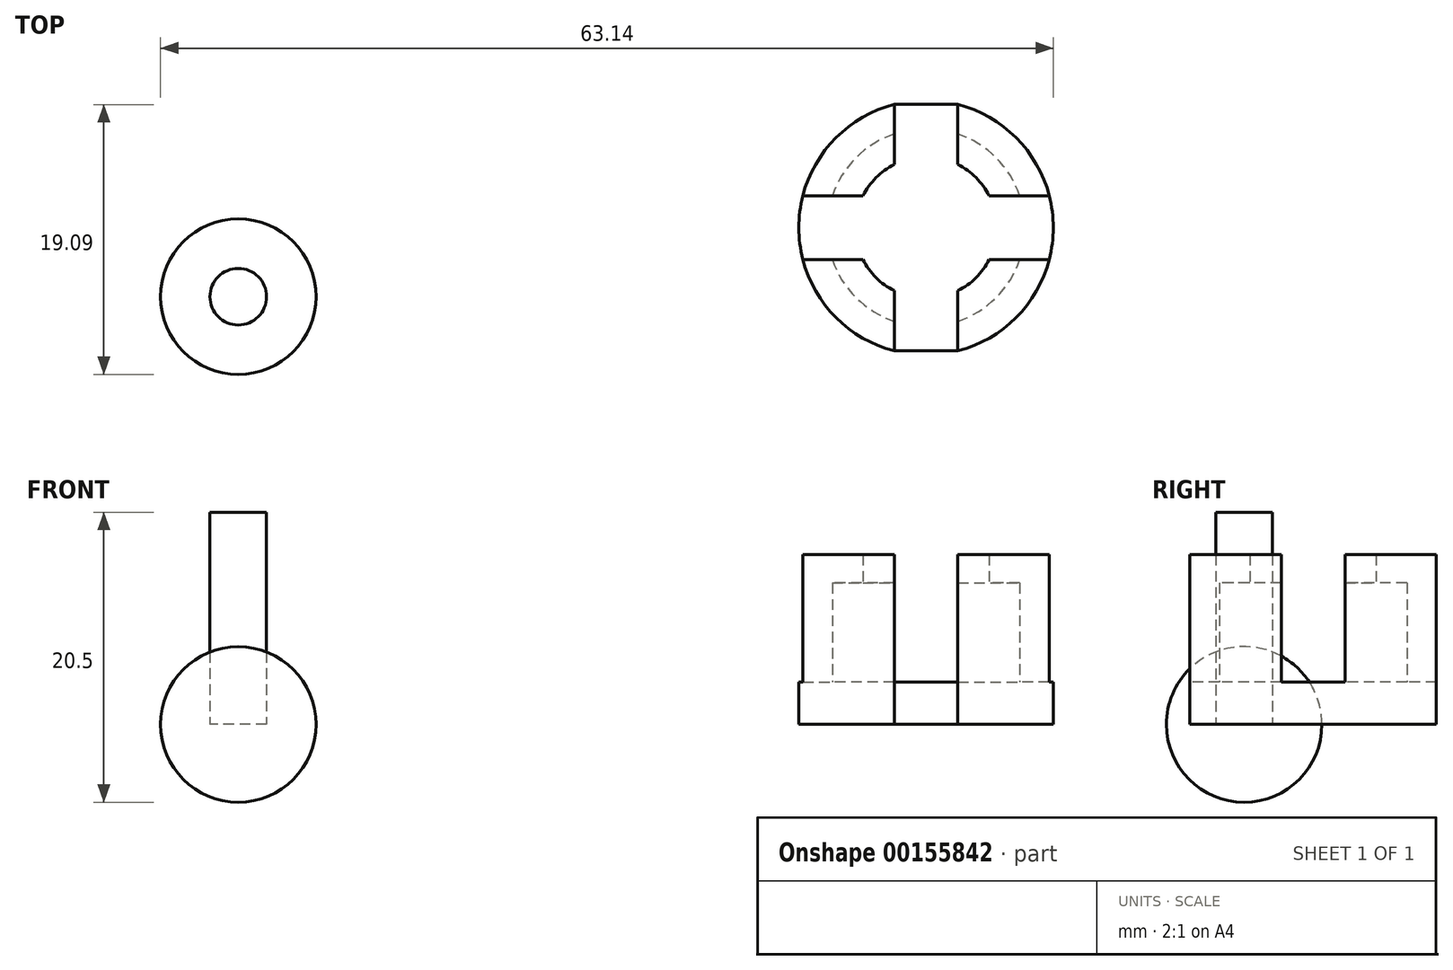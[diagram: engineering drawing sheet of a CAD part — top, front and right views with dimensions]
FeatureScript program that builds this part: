
annotation { "Feature Type Name" : "Feature", "Feature Type Description" : "" }
export const myFeature = defineFeature(function(context is Context, id is Id, definition is map)
    precondition{}
    {
        {
            var Q0;
            Q0=qCreatedBy(makeId("Top.planeOp"),FACE);
            var sketch = newSketch(context, id + "F0", { "sketchPlane" : qUnion([Q0])});
            skArc(sketch, "E0", {"start": v(-2.25, 4.47) * mm, "mid": v(-5, 0) * mm, "end": v(-2.25, -4.47) * mm});
            skArc(sketch, "E1.0", {"start": v(-2.25, 8.71) * mm, "mid": v(-9, 0) * mm, "end": v(-2.25, -8.71) * mm});
            skLineSegment(sketch, "E2", {"start": v(-2.25, 8.71) * mm, "end": v(-2.25, 4.47) * mm});
            skLineSegment(sketch, "E3", {"start": v(-2.25, -4.47) * mm, "end": v(-2.25, -8.71) * mm});
            skLineSegment(sketch, "E4.MirrorCS", {"start": v(2.25, 8.71) * mm, "end": v(2.25, 4.47) * mm});
            skArc(sketch, "E5.MirrorCS", {"start": v(2.25, 8.71) * mm, "mid": v(9, 0) * mm, "end": v(2.25, -8.71) * mm});
            skArc(sketch, "E6.MirrorCS", {"start": v(2.25, 4.47) * mm, "mid": v(5, 0) * mm, "end": v(2.25, -4.47) * mm});
            skLineSegment(sketch, "E7.MirrorCS", {"start": v(2.25, -4.47) * mm, "end": v(2.25, -8.71) * mm});
            skLineSegment(sketch, "E8", {"start": v(-8.71, -2.25) * mm, "end": v(-4.47, -2.25) * mm});
            skLineSegment(sketch, "E9", {"start": v(-8.71, 2.25) * mm, "end": v(-4.47, 2.25) * mm});
            skLineSegment(sketch, "E10.MirrorCS", {"start": v(8.71, -2.25) * mm, "end": v(4.47, -2.25) * mm});
            skLineSegment(sketch, "E11.MirrorCS", {"start": v(8.71, 2.25) * mm, "end": v(4.47, 2.25) * mm});
            skSolve(sketch);
        }
        {
            var Q0;
            Q0=qCreatedBy(makeId("Top.planeOp"),FACE);
            var sketch = newSketch(context, id + "F1", { "sketchPlane" : qUnion([Q0])});
            skArc(sketch, "E12", {"start": v(-48.64, 0.62) * mm, "mid": v(-54.14, -4.88) * mm, "end": v(-48.64, -10.38) * mm});
            skLineSegment(sketch, "E13", {"start": v(-48.64, 0.62) * mm, "end": v(-48.64, -10.38) * mm});
            skSolve(sketch);
        }
        {
            var Q0;
            Q0=makeQuery(id+"F1.imprint","IMPRINT",FACE,{"disambiguationData":[TD([[makeQuery(id+"F1.imprint","IMPRINT",EDGE,{"derivedFrom":sQuery(id+"F1.wireOp",EDGE,"E12")}),1.0]])]});
            var Q1;
            Q1=sQuery(id+"F1.wireOp",EDGE,"E13");
            revolve(context, id + "F2", {"entities" : qUnion([Q0]), "axis" : qUnion([Q1]), "revolveType" : RevolveType.FULL});
        }
        {
            var Q0;
            Q0=qCreatedBy(makeId("Top.planeOp"),FACE);
            var sketch = newSketch(context, id + "F3", { "sketchPlane" : qUnion([Q0])});
            skPoint(sketch, "E14.0", {"position": v(-48.64, -4.88) * mm});
            skCircle(sketch, "E15", {"center": v(-48.64, -4.88) * mm, "radius": 2 * mm});
            skSolve(sketch);
        }
        {
            var Q0;
            Q0=makeQuery(id+"F3.imprint","IMPRINT",FACE,{"disambiguationData":[TD([[makeQuery(id+"F3.imprint","IMPRINT",EDGE,{"derivedFrom":sQuery(id+"F3.wireOp",EDGE,"E15")}),1.0]])]});
            extrude(context, id + "F4", {"entities" : qUnion([Q0]), "depth" : 15 * mm});
        }
        {
            var Q0;
            Q0=qCreatedBy(makeId("Top.planeOp"),FACE);
            var sketch = newSketch(context, id + "F5", { "sketchPlane" : qUnion([Q0])});
            skArc(sketch, "E16.0", {"start": v(-2.25, 4.47) * mm, "mid": v(-5, 0) * mm, "end": v(-2.25, -4.47) * mm});
            skArc(sketch, "E17.0", {"start": v(-2.25, 8.71) * mm, "mid": v(-9, 0) * mm, "end": v(-2.25, -8.71) * mm});
            skLineSegment(sketch, "E18.0", {"start": v(-8.71, 2.25) * mm, "end": v(-4.47, 2.25) * mm});
            skLineSegment(sketch, "E19.0", {"start": v(-8.71, -2.25) * mm, "end": v(-4.47, -2.25) * mm});
            skLineSegment(sketch, "E20.0", {"start": v(-2.25, -4.47) * mm, "end": v(-2.25, -8.71) * mm});
            skLineSegment(sketch, "E21.0", {"start": v(2.25, -4.47) * mm, "end": v(2.25, -8.71) * mm});
            skArc(sketch, "E22.0", {"start": v(2.25, 4.47) * mm, "mid": v(5, 0) * mm, "end": v(2.25, -4.47) * mm});
            skArc(sketch, "E23.0", {"start": v(2.25, 8.71) * mm, "mid": v(9, 0) * mm, "end": v(2.25, -8.71) * mm});
            skLineSegment(sketch, "E24.0", {"start": v(8.71, -2.25) * mm, "end": v(4.47, -2.25) * mm});
            skLineSegment(sketch, "E25.0", {"start": v(8.71, 2.25) * mm, "end": v(4.47, 2.25) * mm});
            skLineSegment(sketch, "E26.0", {"start": v(2.25, 8.71) * mm, "end": v(2.25, 4.47) * mm});
            skLineSegment(sketch, "E27.0", {"start": v(-2.25, 8.71) * mm, "end": v(-2.25, 4.47) * mm});
            skLineSegment(sketch, "E28", {"start": v(-8.71, 2.25) * mm, "end": v(-8.71, -2.25) * mm});
            skLineSegment(sketch, "E29", {"start": v(8.71, 2.25) * mm, "end": v(8.71, -2.25) * mm});
            skLineSegment(sketch, "E30", {"start": v(-2.25, 8.71) * mm, "end": v(2.25, 8.71) * mm});
            skLineSegment(sketch, "E31", {"start": v(-2.25, -8.71) * mm, "end": v(2.25, -8.71) * mm});
            skSolve(sketch);
        }
        {
            var Q0;
            {var subQ2=sQuery(id+"F5.wireOp",EDGE,"E18.0");Q0=makeQuery(id+"F5.imprint","IMPRINT",FACE,{"disambiguationData":[TD([[makeQuery(id+"F5.imprint","IMPRINT",EDGE,{"derivedFrom":subQ2}),1.0]])]});}
            var Q1;
            {var subQ0=sQuery(id+"F0.wireOp",EDGE,"E8");Q1=makeQuery(id+"F0.imprint","IMPRINT",FACE,{"disambiguationData":[TD([[makeQuery(id+"F0.imprint","IMPRINT",EDGE,{"derivedFrom":subQ0}),1.0]])]});}
            var Q2;
            {var subQ2=sQuery(id+"F5.wireOp",EDGE,"E19.0");Q2=makeQuery(id+"F5.imprint","IMPRINT",FACE,{"disambiguationData":[TD([[makeQuery(id+"F5.imprint","IMPRINT",EDGE,{"derivedFrom":subQ2}),-1.0]])]});}
            var Q3;
            {var subQ0=sQuery(id+"F5.wireOp",EDGE,"E21.0");Q3=makeQuery(id+"F5.imprint","IMPRINT",FACE,{"disambiguationData":[TD([[makeQuery(id+"F5.imprint","IMPRINT",EDGE,{"derivedFrom":subQ0}),1.0]])]});}
            var Q4;
            {var subQ0=sQuery(id+"F0.wireOp",EDGE,"E10.MirrorCS");Q4=makeQuery(id+"F0.imprint","IMPRINT",FACE,{"disambiguationData":[TD([[makeQuery(id+"F0.imprint","IMPRINT",EDGE,{"derivedFrom":subQ0}),-1.0]])]});}
            var Q5;
            {var subQ0=sQuery(id+"F0.wireOp",EDGE,"E4.MirrorCS");Q5=makeQuery(id+"F0.imprint","IMPRINT",FACE,{"disambiguationData":[TD([[makeQuery(id+"F0.imprint","IMPRINT",EDGE,{"derivedFrom":subQ0}),1.0]])]});}
            var Q6;
            {var subQ8=sQuery(id+"F5.wireOp",EDGE,"E20.0");Q6=makeQuery(id+"F5.imprint","IMPRINT",FACE,{"disambiguationData":[TD([[makeQuery(id+"F5.imprint","IMPRINT",EDGE,{"derivedFrom":subQ8}),1.0]])]});}
            extrude(context, id + "F6", {"entities" : qUnion([Q0, Q1, Q2, Q3, Q4, Q5, Q6]), "operationType" : NewBodyOperationType.ADD, "depth" : 3 * mm});
        }
        {
            var Q0;
            Q0=makeQuery(id+"F6.boolean.opBoolean","MERGE",FACE,{"derivedFrom":[makeQuery(id+"F6.opExtrude","CAP_FACE",FACE,{"disambiguationData":[OSD([sQuery(id+"F0.wireOp",EDGE,"E0"),sQuery(id+"F0.wireOp",EDGE,"E1.0"),sQuery(id+"F0.wireOp",EDGE,"E8"),sQuery(id+"F0.wireOp",EDGE,"E9")])],"isStart":false}),makeQuery(id+"F6.opExtrude","CAP_FACE",FACE,{"disambiguationData":[OSD([sQuery(id+"F0.wireOp",EDGE,"E4.MirrorCS"),sQuery(id+"F0.wireOp",EDGE,"E5.MirrorCS"),sQuery(id+"F0.wireOp",EDGE,"E6.MirrorCS"),sQuery(id+"F0.wireOp",EDGE,"E10.MirrorCS")])],"isStart":false}),makeQuery(id+"F6.opExtrude","CAP_FACE",FACE,{"disambiguationData":[OSD([sQuery(id+"F5.wireOp",EDGE,"E16.0"),sQuery(id+"F5.wireOp",EDGE,"E17.0"),sQuery(id+"F5.wireOp",EDGE,"E18.0"),sQuery(id+"F5.wireOp",EDGE,"E19.0"),sQuery(id+"F5.wireOp",EDGE,"E22.0"),sQuery(id+"F5.wireOp",EDGE,"E23.0"),sQuery(id+"F5.wireOp",EDGE,"E24.0"),sQuery(id+"F5.wireOp",EDGE,"E26.0"),sQuery(id+"F5.wireOp",EDGE,"E30"),sQuery(id+"F5.wireOp",EDGE,"E31")])],"isStart":false})]});
            var sketch = newSketch(context, id + "F7", { "sketchPlane" : qUnion([Q0])});
            skArc(sketch, "E32.0", {"start": v(-2.25, 4.47) * mm, "mid": v(-5, 0) * mm, "end": v(-2.25, -4.47) * mm});
            skArc(sketch, "E33.0", {"start": v(-2.25, 8.71) * mm, "mid": v(-9, 0) * mm, "end": v(-2.25, -8.71) * mm});
            skLineSegment(sketch, "E34.0", {"start": v(-2.25, 8.71) * mm, "end": v(-2.25, 4.47) * mm});
            skLineSegment(sketch, "E35.0", {"start": v(-2.25, -4.47) * mm, "end": v(-2.25, -8.71) * mm});
            skLineSegment(sketch, "E36.0", {"start": v(2.25, -4.47) * mm, "end": v(2.25, -8.71) * mm});
            skLineSegment(sketch, "E37.0", {"start": v(2.25, 8.71) * mm, "end": v(2.25, 4.47) * mm});
            skArc(sketch, "E38.0", {"start": v(2.25, 8.71) * mm, "mid": v(9, 0) * mm, "end": v(2.25, -8.71) * mm});
            skArc(sketch, "E39.0", {"start": v(2.25, 4.47) * mm, "mid": v(5, 0) * mm, "end": v(2.25, -4.47) * mm});
            skLineSegment(sketch, "E40.0", {"start": v(-8.71, 2.25) * mm, "end": v(-4.47, 2.25) * mm});
            skLineSegment(sketch, "E41.0", {"start": v(-8.71, -2.25) * mm, "end": v(-4.47, -2.25) * mm});
            skLineSegment(sketch, "E42.0", {"start": v(8.71, -2.25) * mm, "end": v(4.47, -2.25) * mm});
            skLineSegment(sketch, "E43.0", {"start": v(8.71, 2.25) * mm, "end": v(4.47, 2.25) * mm});
            skArc(sketch, "E44.0", {"start": v(-2.25, 6.63) * mm, "mid": v(-7, 0) * mm, "end": v(-2.25, -6.63) * mm});
            skArc(sketch, "E45.MirrorCS", {"start": v(2.25, 6.63) * mm, "mid": v(7, 0) * mm, "end": v(2.25, -6.63) * mm});
            skSolve(sketch);
        }
        {
            var Q0;
            {var subQ1=sQuery(id+"F7.wireOp",EDGE,"E33.0");var subQ3=sQuery(id+"F7.wireOp",EDGE,"E40.0");var subQ4=makeQuery(id+"F7.imprint","INTERSECT",VERTEX,{"derivedFrom":[subQ1,subQ3]});Q0=makeQuery(id+"F7.imprint","IMPRINT",FACE,{"disambiguationData":[TD([[makeQuery(id+"F7.imprint","IMPRINT",EDGE,{"disambiguationData":[TD([[subQ4,-1.0]])],"derivedFrom":subQ3}),1.0]])]});}
            var Q1;
            {var subQ0=sQuery(id+"F7.wireOp",EDGE,"E38.0");var subQ5=sQuery(id+"F7.wireOp",EDGE,"E43.0");var subQ6=makeQuery(id+"F7.imprint","INTERSECT",VERTEX,{"derivedFrom":[subQ0,subQ5]});Q1=makeQuery(id+"F7.imprint","IMPRINT",FACE,{"disambiguationData":[TD([[makeQuery(id+"F7.imprint","IMPRINT",EDGE,{"disambiguationData":[TD([[subQ6,-1.0]])],"derivedFrom":subQ5}),-1.0]])]});}
            var Q2;
            {var subQ0=sQuery(id+"F7.wireOp",EDGE,"E38.0");var subQ5=sQuery(id+"F7.wireOp",EDGE,"E42.0");var subQ6=makeQuery(id+"F7.imprint","INTERSECT",VERTEX,{"derivedFrom":[subQ0,subQ5]});Q2=makeQuery(id+"F7.imprint","IMPRINT",FACE,{"disambiguationData":[TD([[makeQuery(id+"F7.imprint","IMPRINT",EDGE,{"disambiguationData":[TD([[subQ6,-1.0]])],"derivedFrom":subQ5}),1.0]])]});}
            var Q3;
            {var subQ1=sQuery(id+"F7.wireOp",EDGE,"E33.0");var subQ3=sQuery(id+"F7.wireOp",EDGE,"E41.0");var subQ4=makeQuery(id+"F7.imprint","INTERSECT",VERTEX,{"derivedFrom":[subQ1,subQ3]});Q3=makeQuery(id+"F7.imprint","IMPRINT",FACE,{"disambiguationData":[TD([[makeQuery(id+"F7.imprint","IMPRINT",EDGE,{"disambiguationData":[TD([[subQ4,-1.0]])],"derivedFrom":subQ3}),-1.0]])]});}
            extrude(context, id + "F8", {"entities" : qUnion([Q0, Q1, Q2, Q3]), "operationType" : NewBodyOperationType.ADD, "depth" : 7 * mm});
        }
        {
            var Q0;
            Q0=makeQuery(id+"F8.opExtrude","CAP_FACE",FACE,{"disambiguationData":[OSD([sQuery(id+"F7.wireOp",EDGE,"E33.0"),sQuery(id+"F7.wireOp",EDGE,"E34.0"),sQuery(id+"F7.wireOp",EDGE,"E40.0"),sQuery(id+"F7.wireOp",EDGE,"E44.0")])],"isStart":false});
            var sketch = newSketch(context, id + "F9", { "sketchPlane" : qUnion([Q0])});
            skArc(sketch, "E46.0", {"start": v(-2.25, 4.47) * mm, "mid": v(-5, 0) * mm, "end": v(-2.25, -4.47) * mm});
            skArc(sketch, "E47.0", {"start": v(2.25, 4.47) * mm, "mid": v(5, 0) * mm, "end": v(2.25, -4.47) * mm});
            skArc(sketch, "E48.0", {"start": v(2.25, 6.63) * mm, "mid": v(4.95, 4.95) * mm, "end": v(6.63, 2.25) * mm});
            skLineSegment(sketch, "E49.0", {"start": v(2.25, 8.71) * mm, "end": v(2.25, 4.47) * mm});
            skLineSegment(sketch, "E50.0", {"start": v(-8.71, 2.25) * mm, "end": v(-4.47, 2.25) * mm});
            skLineSegment(sketch, "E51.0", {"start": v(-2.25, 8.71) * mm, "end": v(-2.25, 4.47) * mm});
            skLineSegment(sketch, "E52.0", {"start": v(8.71, 2.25) * mm, "end": v(4.47, 2.25) * mm});
            skArc(sketch, "E53.0.0", {"start": v(8.71, -2.25) * mm, "mid": v(9, 0) * mm, "end": v(8.71, 2.25) * mm});
            skLineSegment(sketch, "E53.0.1", {"start": v(8.71, 2.25) * mm, "end": v(6.63, 2.25) * mm});
            skArc(sketch, "E53.0.2", {"start": v(6.63, 2.25) * mm, "mid": v(4.95, 4.95) * mm, "end": v(2.25, 6.63) * mm});
            skLineSegment(sketch, "E53.0.3", {"start": v(2.25, 6.63) * mm, "end": v(2.25, 8.71) * mm});
            skLineSegment(sketch, "E53.0.4", {"start": v(2.25, 8.71) * mm, "end": v(-2.25, 8.71) * mm});
            skLineSegment(sketch, "E53.0.5", {"start": v(-2.25, 8.71) * mm, "end": v(-2.25, 6.63) * mm});
            skArc(sketch, "E53.0.6", {"start": v(-2.25, 6.63) * mm, "mid": v(-4.95, 4.95) * mm, "end": v(-6.63, 2.25) * mm});
            skLineSegment(sketch, "E53.0.7", {"start": v(-6.63, 2.25) * mm, "end": v(-8.71, 2.25) * mm});
            skArc(sketch, "E53.0.8", {"start": v(-8.71, 2.25) * mm, "mid": v(-9, 0) * mm, "end": v(-8.71, -2.25) * mm});
            skLineSegment(sketch, "E53.0.9", {"start": v(-8.71, -2.25) * mm, "end": v(-6.63, -2.25) * mm});
            skArc(sketch, "E53.0.10", {"start": v(-6.63, -2.25) * mm, "mid": v(-4.95, -4.95) * mm, "end": v(-2.25, -6.63) * mm});
            skLineSegment(sketch, "E53.0.11", {"start": v(-2.25, -6.63) * mm, "end": v(-2.25, -8.71) * mm});
            skLineSegment(sketch, "E53.0.12", {"start": v(-2.25, -8.71) * mm, "end": v(2.25, -8.71) * mm});
            skLineSegment(sketch, "E53.0.13", {"start": v(2.25, -8.71) * mm, "end": v(2.25, -6.63) * mm});
            skArc(sketch, "E53.0.14", {"start": v(2.25, -6.63) * mm, "mid": v(4.95, -4.95) * mm, "end": v(6.63, -2.25) * mm});
            skLineSegment(sketch, "E53.0.15", {"start": v(6.63, -2.25) * mm, "end": v(8.71, -2.25) * mm});
            skLineSegment(sketch, "E54.0", {"start": v(8.71, -2.25) * mm, "end": v(4.47, -2.25) * mm});
            skLineSegment(sketch, "E55.0", {"start": v(2.25, -4.47) * mm, "end": v(2.25, -8.71) * mm});
            skLineSegment(sketch, "E56.0", {"start": v(-2.25, -4.47) * mm, "end": v(-2.25, -8.71) * mm});
            skLineSegment(sketch, "E57.0", {"start": v(-8.71, -2.25) * mm, "end": v(-4.47, -2.25) * mm});
            skSolve(sketch);
        }
        {
            var Q0;
            Q0=makeQuery(id+"F9.imprint","IMPRINT",FACE,{"disambiguationData":[TD([[makeQuery(id+"F9.imprint","IMPRINT",EDGE,{"derivedFrom":sQuery(id+"F9.wireOp",EDGE,"E53.0.5")}),-1.0]])]});
            var Q1;
            {var subQ2=sQuery(id+"F9.wireOp",EDGE,"E50.0");Q1=makeQuery(id+"F9.imprint","IMPRINT",FACE,{"disambiguationData":[TD([[makeQuery(id+"F9.imprint","IMPRINT",EDGE,{"derivedFrom":subQ2}),1.0]])]});}
            var Q2;
            Q2=makeQuery(id+"F8.opExtrude","CAP_FACE",FACE,{"disambiguationData":[OSD([sQuery(id+"F7.wireOp",EDGE,"E37.0"),sQuery(id+"F7.wireOp",EDGE,"E38.0"),sQuery(id+"F7.wireOp",EDGE,"E43.0"),sQuery(id+"F7.wireOp",EDGE,"E45.MirrorCS")])],"isStart":false});
            var Q3;
            {var subQ0=sQuery(id+"F9.wireOp",EDGE,"E49.0");Q3=makeQuery(id+"F9.imprint","IMPRINT",FACE,{"disambiguationData":[TD([[makeQuery(id+"F9.imprint","IMPRINT",EDGE,{"derivedFrom":subQ0}),1.0]])]});}
            var Q4;
            Q4=makeQuery(id+"F8.opExtrude","CAP_FACE",FACE,{"disambiguationData":[OSD([sQuery(id+"F7.wireOp",EDGE,"E36.0"),sQuery(id+"F7.wireOp",EDGE,"E38.0"),sQuery(id+"F7.wireOp",EDGE,"E42.0"),sQuery(id+"F7.wireOp",EDGE,"E45.MirrorCS")])],"isStart":false});
            var Q5;
            {var subQ5=sQuery(id+"F9.wireOp",EDGE,"E53.0.14");Q5=makeQuery(id+"F9.imprint","IMPRINT",FACE,{"disambiguationData":[TD([[makeQuery(id+"F9.imprint","IMPRINT",EDGE,{"derivedFrom":subQ5}),1.0]])]});}
            var Q6;
            {var subQ5=sQuery(id+"F9.wireOp",EDGE,"E53.0.10");Q6=makeQuery(id+"F9.imprint","IMPRINT",FACE,{"disambiguationData":[TD([[makeQuery(id+"F9.imprint","IMPRINT",EDGE,{"derivedFrom":subQ5}),1.0]])]});}
            var Q7;
            Q7=makeQuery(id+"F8.opExtrude","CAP_FACE",FACE,{"disambiguationData":[OSD([sQuery(id+"F7.wireOp",EDGE,"E33.0"),sQuery(id+"F7.wireOp",EDGE,"E35.0"),sQuery(id+"F7.wireOp",EDGE,"E41.0"),sQuery(id+"F7.wireOp",EDGE,"E44.0")])],"isStart":false});
            extrude(context, id + "F10", {"entities" : qUnion([Q0, Q1, Q2, Q3, Q4, Q5, Q6, Q7]), "operationType" : NewBodyOperationType.ADD, "depth" : 2 * mm});
        }
    });
